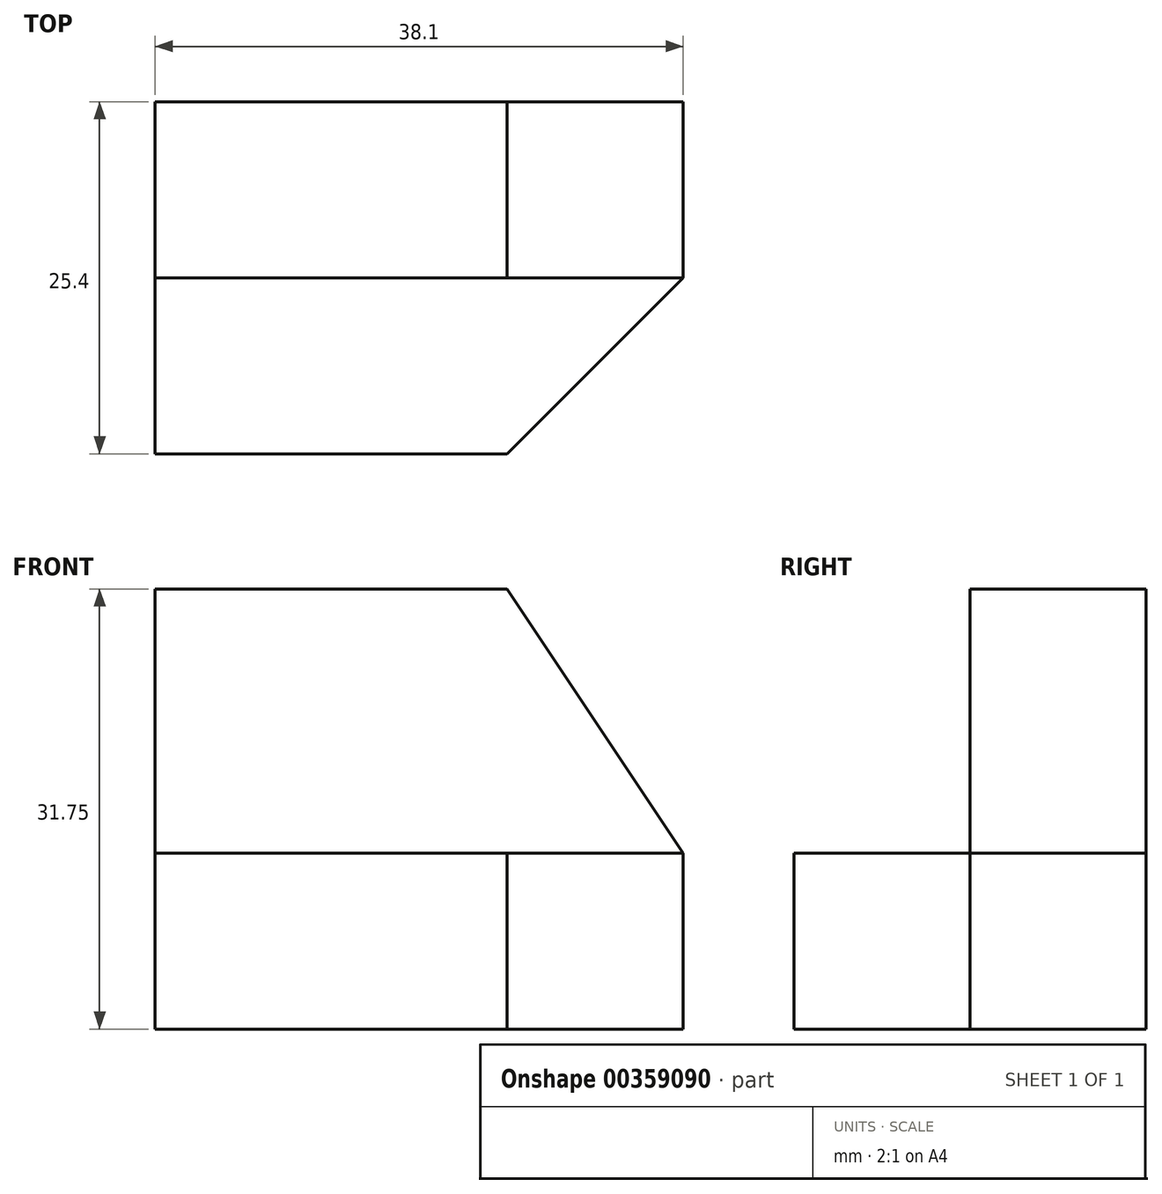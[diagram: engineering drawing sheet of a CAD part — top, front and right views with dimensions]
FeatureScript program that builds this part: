
annotation { "Feature Type Name" : "Feature", "Feature Type Description" : "" }
export const myFeature = defineFeature(function(context is Context, id is Id, definition is map)
    precondition{}
    {
        {
            var Q0;
            Q0=qCreatedBy(makeId("Right.planeOp"),FACE);
            var sketch = newSketch(context, id + "F0", { "sketchPlane" : qUnion([Q0])});
            skLineSegment(sketch, "E0", {"start": v(0, 0) * mm, "end": v(0, 12.7) * mm});
            skLineSegment(sketch, "E1", {"start": v(0, 12.7) * mm, "end": v(12.7, 12.7) * mm});
            skLineSegment(sketch, "E2", {"start": v(12.7, 12.7) * mm, "end": v(12.7, 31.75) * mm});
            skLineSegment(sketch, "E3", {"start": v(12.7, 31.75) * mm, "end": v(25.4, 31.75) * mm});
            skLineSegment(sketch, "E4", {"start": v(25.4, 31.75) * mm, "end": v(25.4, 0) * mm});
            skLineSegment(sketch, "E5", {"start": v(25.4, 0) * mm, "end": v(0, 0) * mm});
            skSolve(sketch);
        }
        {
            var Q0;
            Q0 = qSketchRegion(id + "F0", true);
            extrude(context, id + "F1", {"entities" : qUnion([Q0]), "depth" : 38.1 * mm});
        }
        {
            var Q0;
            Q0=makeQuery(id+"F1.opExtrude","SWEPT_FACE",FACE,{"disambiguationData":[OSD([sQuery(id+"F0.wireOp",EDGE,"E1")])]});
            var sketch = newSketch(context, id + "F2", { "sketchPlane" : qUnion([Q0])});
            skLineSegment(sketch, "E6", {"start": v(38.1, 12.7) * mm, "end": v(25.4, 0) * mm});
            skLineSegment(sketch, "E7", {"start": v(38.1, 12.7) * mm, "end": v(38.1, 0) * mm});
            skLineSegment(sketch, "E8", {"start": v(38.1, 0) * mm, "end": v(25.4, 0) * mm});
            skSolve(sketch);
        }
        {
            var Q0;
            Q0 = qSketchRegion(id + "F2", true);
            extrude(context, id + "F3", {"entities" : qUnion([Q0]), "operationType" : NewBodyOperationType.REMOVE, "oppositeDirection" : true, "depth" : 25.4 * mm});
        }
        {
            var Q0;
            Q0=makeQuery(id+"F1.opExtrude","SWEPT_FACE",FACE,{"disambiguationData":[OSD([sQuery(id+"F0.wireOp",EDGE,"E2")])]});
            var sketch = newSketch(context, id + "F4", { "sketchPlane" : qUnion([Q0])});
            skLineSegment(sketch, "E9", {"start": v(38.1, 31.75) * mm, "end": v(38.1, 12.7) * mm});
            skLineSegment(sketch, "E10", {"start": v(38.1, 12.7) * mm, "end": v(25.4, 31.75) * mm});
            skLineSegment(sketch, "E11", {"start": v(25.4, 31.75) * mm, "end": v(38.1, 31.75) * mm});
            skSolve(sketch);
        }
        {
            var Q0;
            Q0 = qSketchRegion(id + "F4", true);
            extrude(context, id + "F5", {"entities" : qUnion([Q0]), "operationType" : NewBodyOperationType.REMOVE, "oppositeDirection" : true, "depth" : 25.4 * mm});
        }
    });
